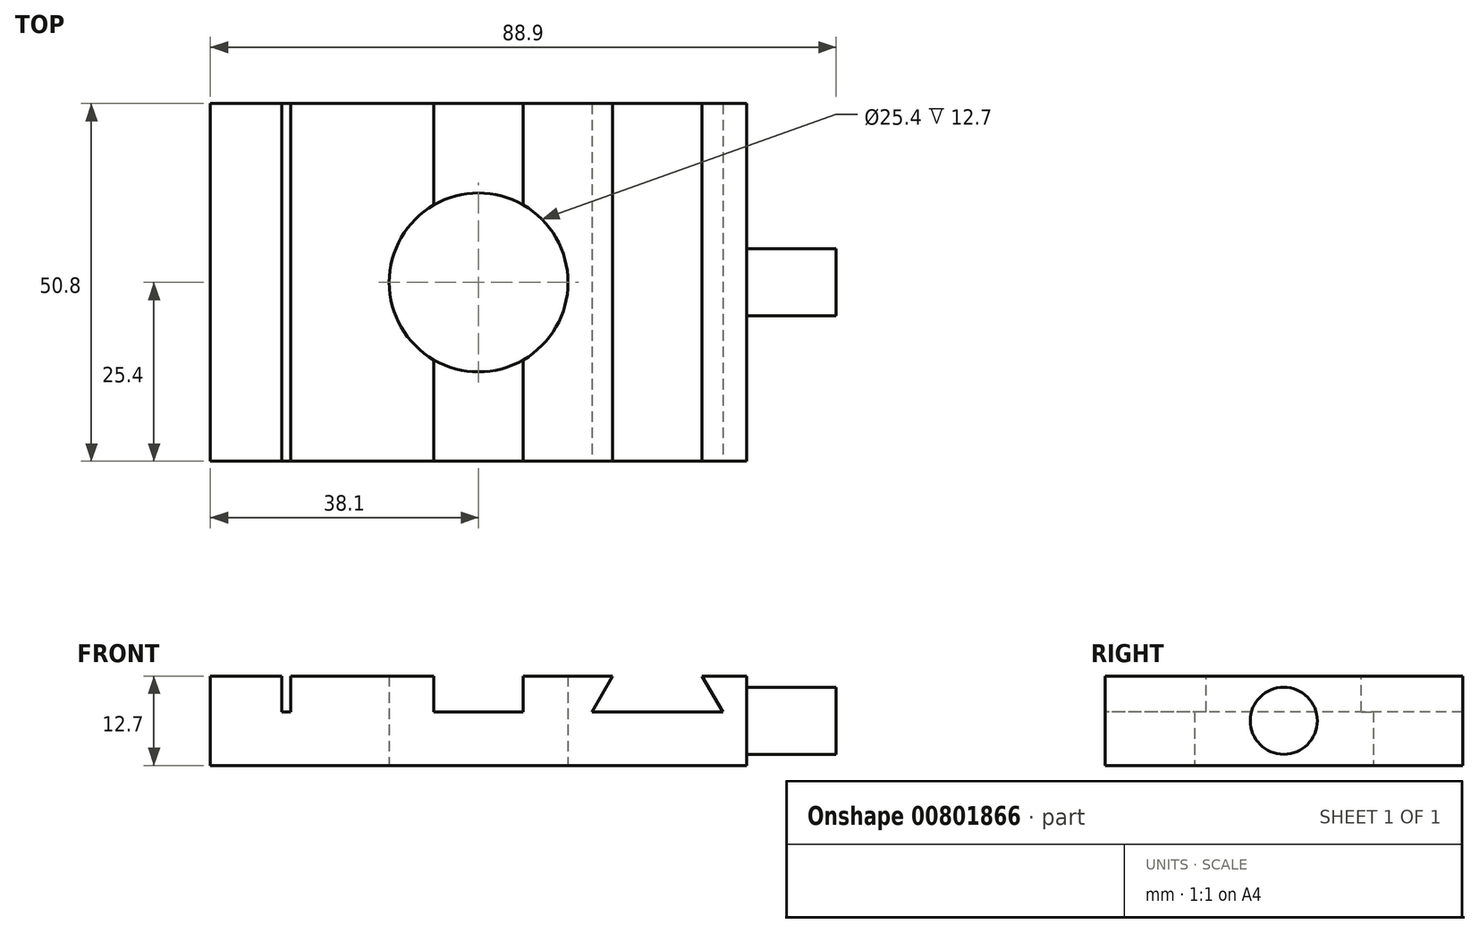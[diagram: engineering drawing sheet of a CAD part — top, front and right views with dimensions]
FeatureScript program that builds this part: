
annotation { "Feature Type Name" : "Feature", "Feature Type Description" : "" }
export const myFeature = defineFeature(function(context is Context, id is Id, definition is map)
    precondition{}
    {
        {
            var Q0;
            Q0=qCreatedBy(makeId("Top.planeOp"),FACE);
            var sketch = newSketch(context, id + "F0", { "sketchPlane" : qUnion([Q0])});
            skLineSegment(sketch, "E0.bottom", {"start": v(-38.1, 25.4) * mm, "end": v(38.1, 25.4) * mm});
            skLineSegment(sketch, "E0.top", {"start": v(-38.1, -25.4) * mm, "end": v(38.1, -25.4) * mm});
            skLineSegment(sketch, "E0.left", {"start": v(-38.1, 25.4) * mm, "end": v(-38.1, -25.4) * mm});
            skLineSegment(sketch, "E0.right", {"start": v(38.1, 25.4) * mm, "end": v(38.1, -25.4) * mm});
            skPoint(sketch, "E0.middle", {"position": v(0, 0) * mm});
            skCircle(sketch, "E1", {"center": v(0, 0) * mm, "radius": 12.7 * mm});
            skSolve(sketch);
        }
        {
            var Q0;
            Q0=makeQuery(id+"F0.imprint","IMPRINT",FACE,{"disambiguationData":[TD([[makeQuery(id+"F0.imprint","IMPRINT",EDGE,{"derivedFrom":sQuery(id+"F0.wireOp",EDGE,"E0.bottom")}),-1.0]])]});
            extrude(context, id + "F1", {"entities" : qUnion([Q0]), "depth" : 12.7 * mm, "offsetDistance" : 25 * mm});
        }
        {
            var Q0;
            Q0=makeQuery(id+"F1.opExtrude","CAP_FACE",FACE,{"disambiguationData":[OSD([sQuery(id+"F0.wireOp",EDGE,"E0.bottom"),sQuery(id+"F0.wireOp",EDGE,"E0.top"),sQuery(id+"F0.wireOp",EDGE,"E0.left"),sQuery(id+"F0.wireOp",EDGE,"E0.right"),sQuery(id+"F0.wireOp",EDGE,"E1")])],"isStart":false});
            var sketch = newSketch(context, id + "F2", { "sketchPlane" : qUnion([Q0])});
            skLineSegment(sketch, "E2.bottom", {"start": v(-27.94, 25.4) * mm, "end": v(-26.67, 25.4) * mm});
            skLineSegment(sketch, "E2.top", {"start": v(-27.94, -25.4) * mm, "end": v(-26.67, -25.4) * mm});
            skLineSegment(sketch, "E2.left", {"start": v(-27.94, 25.4) * mm, "end": v(-27.94, -25.4) * mm});
            skLineSegment(sketch, "E2.right", {"start": v(-26.67, 25.4) * mm, "end": v(-26.67, -25.4) * mm});
            skLineSegment(sketch, "E3", {"start": v(-6.35, 25.4) * mm, "end": v(-6.35, -25.4) * mm});
            skLineSegment(sketch, "E4", {"start": v(-6.35, -25.4) * mm, "end": v(6.35, -25.4) * mm});
            skLineSegment(sketch, "E5", {"start": v(6.35, -25.4) * mm, "end": v(6.35, 25.4) * mm});
            skLineSegment(sketch, "E6", {"start": v(6.35, 25.4) * mm, "end": v(-6.35, 25.4) * mm});
            skPoint(sketch, "E7", {"position": v(0, 0) * mm});
            skLineSegment(sketch, "E8", {"start": v(0, 25.4) * mm, "end": v(0, -25.4) * mm, "construction": true});
            skSolve(sketch);
        }
        {
            var Q0;
            {var subQ0=sQuery(id+"F2.wireOp",EDGE,"E4");Q0=makeQuery(id+"F2.imprint","IMPRINT",FACE,{"disambiguationData":[TD([[makeQuery(id+"F2.imprint","IMPRINT",EDGE,{"derivedFrom":subQ0}),1.0]])]});}
            var Q1;
            {var subQ0=sQuery(id+"F2.wireOp",EDGE,"E6");Q1=makeQuery(id+"F2.imprint","IMPRINT",FACE,{"disambiguationData":[TD([[makeQuery(id+"F2.imprint","IMPRINT",EDGE,{"derivedFrom":subQ0}),-1.0]])]});}
            var Q2;
            Q2=makeQuery(id+"F2.imprint","IMPRINT",FACE,{"disambiguationData":[TD([[makeQuery(id+"F2.imprint","IMPRINT",EDGE,{"derivedFrom":sQuery(id+"F2.wireOp",EDGE,"E2.bottom")}),-1.0]])]});
            extrude(context, id + "F3", {"entities" : qUnion([Q0, Q1, Q2]), "operationType" : NewBodyOperationType.REMOVE, "oppositeDirection" : true, "depth" : 5.08 * mm, "offsetDistance" : 25.4 * mm});
        }
        {
            var Q0;
            Q0=makeQuery(id+"F1.opExtrude","SWEPT_FACE",FACE,{"disambiguationData":[OSD([sQuery(id+"F0.wireOp",EDGE,"E0.top")])]});
            var sketch = newSketch(context, id + "F4", { "sketchPlane" : qUnion([Q0])});
            skLineSegment(sketch, "E9", {"start": v(19.05, 12.7) * mm, "end": v(16.12, 7.62) * mm});
            skLineSegment(sketch, "E10", {"start": v(16.12, 7.62) * mm, "end": v(34.68, 7.62) * mm});
            skLineSegment(sketch, "E11", {"start": v(34.68, 7.62) * mm, "end": v(31.75, 12.7) * mm});
            skLineSegment(sketch, "E12", {"start": v(31.75, 12.7) * mm, "end": v(19.05, 12.7) * mm});
            skLineSegment(sketch, "E13", {"start": v(25.4, 7.62) * mm, "end": v(25.4, 12.7) * mm, "construction": true});
            skSolve(sketch);
        }
        {
            var Q0;
            Q0=makeQuery(id+"F4.imprint","IMPRINT",FACE,{"disambiguationData":[TD([[makeQuery(id+"F4.imprint","IMPRINT",EDGE,{"derivedFrom":sQuery(id+"F4.wireOp",EDGE,"E9")}),1.0]])]});
            extrude(context, id + "F5", {"entities" : qUnion([Q0]), "operationType" : NewBodyOperationType.REMOVE, "endBound" : BoundingType.THROUGH_ALL, "oppositeDirection" : true, "depth" : 25.4 * mm, "offsetDistance" : 25.4 * mm});
        }
        {
            var Q0;
            Q0=makeQuery(id+"F1.opExtrude","SWEPT_FACE",FACE,{"disambiguationData":[OSD([sQuery(id+"F0.wireOp",EDGE,"E0.right")])]});
            var sketch = newSketch(context, id + "F6", { "sketchPlane" : qUnion([Q0])});
            skCircle(sketch, "E14", {"center": v(0, 6.35) * mm, "radius": 4.76 * mm});
            skPoint(sketch, "E14.centerSnap0", {"position": v(-25.4, 6.35) * mm});
            skPoint(sketch, "E14.centerSnap1", {"position": v(0, 12.7) * mm});
            skSolve(sketch);
        }
        {
            var Q0;
            Q0=makeQuery(id+"F6.imprint","IMPRINT",FACE,{"disambiguationData":[TD([[makeQuery(id+"F6.imprint","IMPRINT",EDGE,{"derivedFrom":sQuery(id+"F6.wireOp",EDGE,"E14")}),1.0]])]});
            extrude(context, id + "F7", {"entities" : qUnion([Q0]), "operationType" : NewBodyOperationType.ADD, "depth" : 12.7 * mm, "offsetDistance" : 25.4 * mm});
        }
    });
